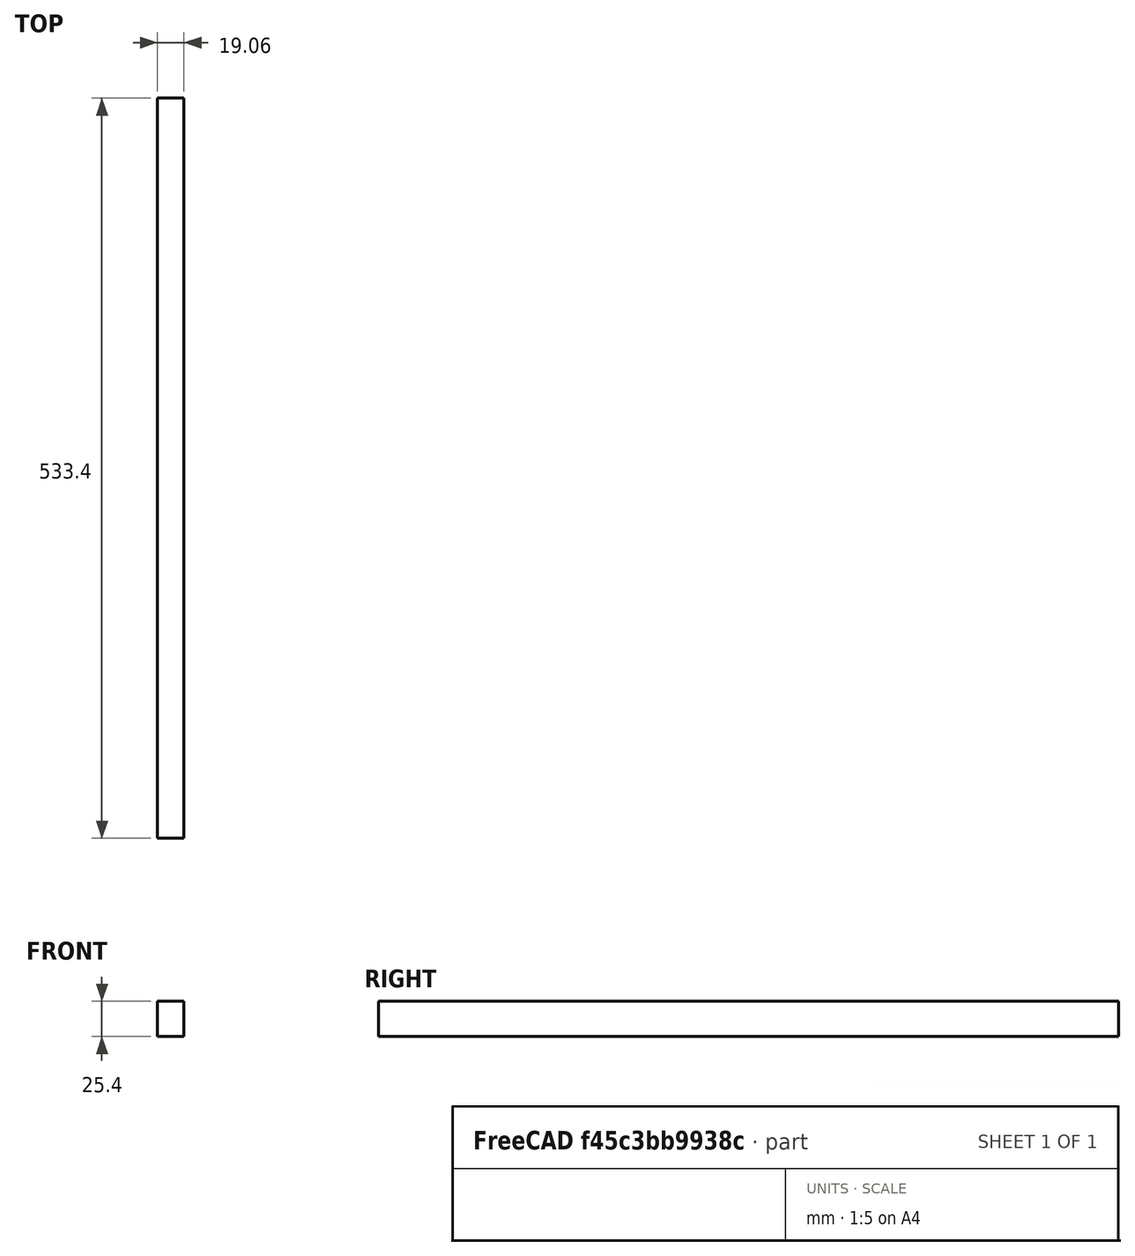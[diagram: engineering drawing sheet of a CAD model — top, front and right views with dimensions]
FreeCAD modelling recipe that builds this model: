
FCSTD DOCUMENT  (FreeCAD 0.20R29603 (Git))
Label: stop-cleat
License: All rights reserved
LicenseURL: http://en.wikipedia.org/wiki/All_rights_reserved
objects: TechDraw::DrawProjGroupItem×3, TechDraw::DrawViewDimension×3, Sketcher::SketchObject×1, PartDesign::Pad×1, PartDesign::Body×1, TechDraw::DrawSVGTemplate×1, TechDraw::DrawProjGroup×1, TechDraw::DrawPage×1
note: 4 computed .brp shape members not serialized (recipe doc carries the construction recipe); baked Part::Feature solids carry a one-line shape summary decoded from their .brp

FEATURE [Sketcher::SketchObject] Sketch
  FullyConstrained = true
  MapMode = 5
  Support = -> [XY_Plane]
  sketch-geometry (5):
    g0: LineSegment StartX=-9.525 StartY=-266.7 StartZ=0 EndX=-9.525 EndY=266.7 EndZ=0
    g1: LineSegment StartX=-9.525 StartY=266.7 StartZ=0 EndX=9.525 EndY=266.7 EndZ=0
    g2: LineSegment StartX=9.525 StartY=266.7 StartZ=0 EndX=9.525 EndY=-266.7 EndZ=0
    g3: LineSegment StartX=9.525 StartY=-266.7 StartZ=0 EndX=-9.525 EndY=-266.7 EndZ=0
    g4: GeomPoint X=0 Y=0 Z=0
  constraints (12):
    c: Coincident(g0,g1)
    c: Coincident(g1,g2)
    c: Coincident(g2,g3)
    c: Coincident(g3,g0)
    c: Horizontal(g1)
    c: Horizontal(g3)
    c: Vertical(g0)
    c: Vertical(g2)
    c: Symmetric(g1,g0,g4)
    c: Coincident(g-1,g4)
    c: DistanceY(g2,g2) = 533.4
    c: DistanceX(g3,g3) = 19.05
FEATURE [PartDesign::Pad] Pad
  Direction = (0,0,1)
  Length = 25.4
  Length2 = 10
  Profile = -> Sketch
  ReferenceAxis = -> Sketch [N_Axis]
  Type = 0
FEATURE [PartDesign::Body] Body
  Group = -> [Sketch,Pad]
  Origin = -> Origin
  Tip = -> Pad
FEATURE [TechDraw::DrawSVGTemplate] Template
  Height = 297
  Orientation = 1
  Width = 420
FEATURE [TechDraw::DrawProjGroupItem] ProjItem  label="Front"
  CoarseView = false
  Direction = (-1,0,0)
  Focus = 100
  HardHidden = false
  IsoCount = 0
  IsoHidden = false
  IsoVisible = false
  LockPosition = true
  Perspective = false
  Rotation = 0
  RotationVector = (0,-1,0)
  Scale = 0.5
  ScaleType = 2
  SeamHidden = false
  SeamVisible = true
  SmoothHidden = false
  SmoothVisible = true
  Source = -> [Body]
  Type = 0
  X = 0
  XDirection = (0,-1,0)
  Y = 0
FEATURE [TechDraw::DrawProjGroupItem] ProjItem001  label="Left"
  CoarseView = false
  Direction = (-1e-16,1,0)
  Focus = 100
  HardHidden = false
  IsoCount = 0
  IsoHidden = false
  IsoVisible = false
  LockPosition = false
  Perspective = false
  Rotation = 0
  RotationVector = (1,0,0)
  Scale = 0.5
  ScaleType = 2
  SeamHidden = false
  SeamVisible = true
  SmoothHidden = false
  SmoothVisible = true
  Source = -> [Body]
  Type = 1
  X = 200.019
  XDirection = (-1,-1e-16,0)
  Y = 0
FEATURE [TechDraw::DrawProjGroupItem] ProjItem002  label="FrontTopRight"
  CoarseView = false
  Direction = (-0.57735,-0.57735,0.57735)
  Focus = 100
  HardHidden = false
  IsoCount = 0
  IsoHidden = false
  IsoVisible = false
  LockPosition = false
  Perspective = false
  Rotation = 0
  RotationVector = (1,0,0)
  Scale = 0.5
  ScaleType = 2
  SeamHidden = false
  SeamVisible = true
  SmoothHidden = false
  SmoothVisible = true
  Source = -> [Body]
  Type = 7
  X = 155.908
  XDirection = (0.707107,-0.707107,0)
  Y = 112.791
FEATURE [TechDraw::DrawProjGroup] ProjGroup
  Anchor = -> ProjItem
  AutoDistribute = true
  LockPosition = false
  ProjectionType = 0
  Rotation = 0
  Scale = 0.5
  ScaleType = 0
  Source = -> [Body]
  Views = -> [ProjItem,ProjItem001,ProjItem002]
  X = 148.573
  Y = 110.699
  spacingX = 15.0812
  spacingY = 15.0812
FEATURE [TechDraw::DrawViewDimension] Dimension
  AngleOverride = false
  Arbitrary = false
  ArbitraryTolerances = false
  EqualTolerance = true
  ExtensionAngle = 0
  FormatSpec = %.2w
  FormatSpecOverTolerance = %+.2w
  FormatSpecUnderTolerance = %+.2w
  Inverted = false
  LineAngle = 0
  LockPosition = false
  MeasureType = 1
  OverTolerance = 0
  References2D = -> [ProjItem001]
  Rotation = 0
  Scale = 0.5
  ScaleType = 0
  TheoreticalExact = false
  Type = 2
  UnderTolerance = 0
  X = 12.9407
  Y = -18.623
FEATURE [TechDraw::DrawViewDimension] Dimension001
  AngleOverride = false
  Arbitrary = false
  ArbitraryTolerances = false
  EqualTolerance = true
  ExtensionAngle = 0
  FormatSpec = %.2w
  FormatSpecOverTolerance = %+.2w
  FormatSpecUnderTolerance = %+.2w
  Inverted = false
  LineAngle = 0
  LockPosition = false
  MeasureType = 1
  OverTolerance = 0
  References2D = -> [ProjItem001]
  Rotation = 0
  Scale = 0.5
  ScaleType = 0
  TheoreticalExact = false
  Type = 1
  UnderTolerance = 0
  X = 15.7505
  Y = 28.315
FEATURE [TechDraw::DrawViewDimension] Dimension002
  AngleOverride = false
  Arbitrary = false
  ArbitraryTolerances = false
  EqualTolerance = true
  ExtensionAngle = 0
  FormatSpec = %.2w
  FormatSpecOverTolerance = %+.2w
  FormatSpecUnderTolerance = %+.2w
  Inverted = false
  LineAngle = 0
  LockPosition = false
  MeasureType = 1
  OverTolerance = 0
  References2D = -> [ProjItem]
  Rotation = 0
  Scale = 0.5
  ScaleType = 0
  TheoreticalExact = false
  Type = 1
  UnderTolerance = 0
  X = 3.33185
  Y = 21.6513
FEATURE [TechDraw::DrawPage] Page
  KeepUpdated = true
  NextBalloonIndex = 1
  ProjectionType = 0
  Scale = 0.5
  Template = -> Template
  Views = -> [ProjGroup,Dimension,Dimension001,Dimension002]
